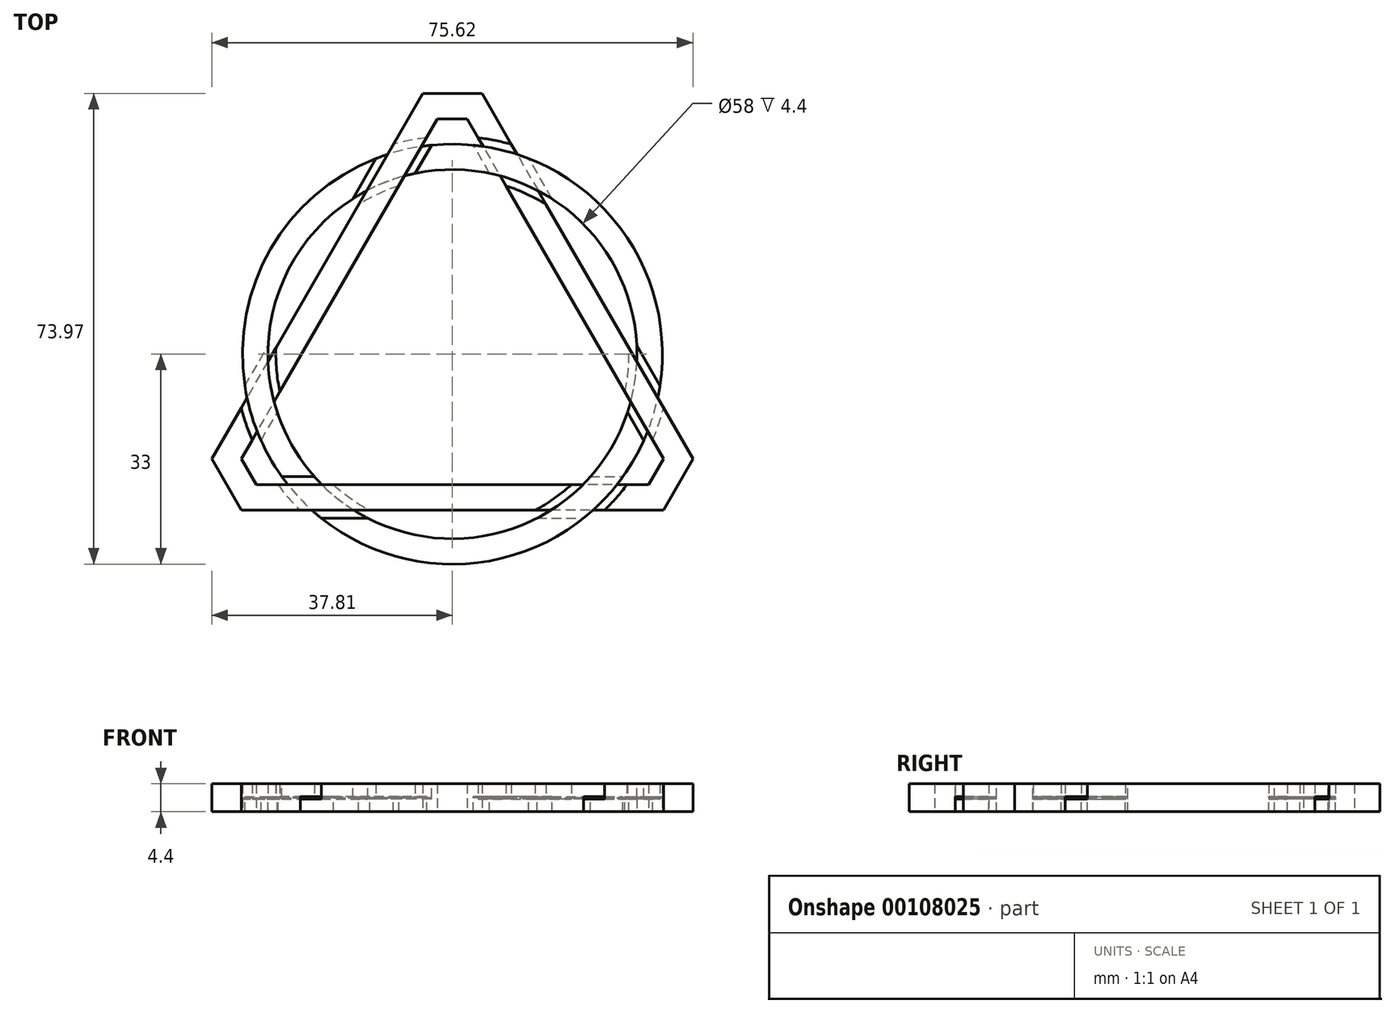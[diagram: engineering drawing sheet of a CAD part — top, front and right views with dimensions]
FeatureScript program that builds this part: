
annotation { "Feature Type Name" : "Feature", "Feature Type Description" : "" }
export const myFeature = defineFeature(function(context is Context, id is Id, definition is map)
    precondition{}
    {
        {
            var Q0;
            Q0=qCreatedBy(makeId("Top.planeOp"),FACE);
            var sketch = newSketch(context, id + "F0", { "sketchPlane" : qUnion([Q0])});
            skCircle(sketch, "E0", {"center": v(0, 0) * mm, "radius": 29 * mm});
            skCircle(sketch, "E1", {"center": v(0, 0) * mm, "radius": 33 * mm});
            skCircle(sketch, "E2", {"center": v(0, 0) * mm, "radius": 27.75 * mm, "construction": true});
            skCircle(sketch, "E3", {"center": v(0, 0) * mm, "radius": 34.25 * mm, "construction": true});
            skLineSegment(sketch, "E4", {"start": v(0, 45.03) * mm, "end": v(39, -22.52) * mm, "construction": true});
            skLineSegment(sketch, "E5", {"start": v(39, -22.52) * mm, "end": v(-39, -22.52) * mm, "construction": true});
            skLineSegment(sketch, "E6", {"start": v(-39, -22.52) * mm, "end": v(0, 45.03) * mm, "construction": true});
            skLineSegment(sketch, "E7", {"start": v(-3.5, 38.97) * mm, "end": v(3.5, 38.97) * mm, "construction": true});
            skLineSegment(sketch, "E8", {"start": v(35.5, -16.45) * mm, "end": v(32, -22.52) * mm, "construction": true});
            skLineSegment(sketch, "E9", {"start": v(-35.5, -16.45) * mm, "end": v(-32, -22.52) * mm, "construction": true});
            skLineSegment(sketch, "E10", {"start": v(39, -22.52) * mm, "end": v(-19.5, 11.26) * mm, "construction": true});
            skLineSegment(sketch, "E11", {"start": v(3.5, 38.97) * mm, "end": v(35.5, -16.45) * mm, "construction": true});
            skLineSegment(sketch, "E12", {"start": v(32, -22.52) * mm, "end": v(-32, -22.52) * mm, "construction": true});
            skLineSegment(sketch, "E13", {"start": v(-35.5, -16.45) * mm, "end": v(-3.5, 38.97) * mm, "construction": true});
            skLineSegment(sketch, "E14.0", {"start": v(-33.2, -16.45) * mm, "end": v(-2.35, 36.97) * mm});
            skLineSegment(sketch, "E14.1", {"start": v(2.35, 36.97) * mm, "end": v(33.2, -16.45) * mm});
            skLineSegment(sketch, "E14.2", {"start": v(33.2, -16.45) * mm, "end": v(30.85, -20.52) * mm});
            skLineSegment(sketch, "E14.3", {"start": v(-2.35, 36.97) * mm, "end": v(2.35, 36.97) * mm});
            skLineSegment(sketch, "E14.4", {"start": v(30.85, -20.52) * mm, "end": v(-30.85, -20.52) * mm});
            skLineSegment(sketch, "E14.5", {"start": v(-33.2, -16.45) * mm, "end": v(-30.85, -20.52) * mm});
            skLineSegment(sketch, "E15.0", {"start": v(-31.75, -16.45) * mm, "end": v(-1.62, 35.72) * mm, "construction": true});
            skLineSegment(sketch, "E15.1", {"start": v(1.62, 35.72) * mm, "end": v(31.75, -16.45) * mm, "construction": true});
            skLineSegment(sketch, "E15.2", {"start": v(31.75, -16.45) * mm, "end": v(30.12, -19.27) * mm, "construction": true});
            skLineSegment(sketch, "E15.3", {"start": v(-1.62, 35.72) * mm, "end": v(1.62, 35.72) * mm, "construction": true});
            skLineSegment(sketch, "E15.4", {"start": v(30.12, -19.27) * mm, "end": v(-30.12, -19.27) * mm, "construction": true});
            skLineSegment(sketch, "E15.5", {"start": v(-31.75, -16.45) * mm, "end": v(-30.12, -19.27) * mm, "construction": true});
            skLineSegment(sketch, "E16.0", {"start": v(-37.8, -16.45) * mm, "end": v(-33.15, -24.52) * mm});
            skLineSegment(sketch, "E16.1", {"start": v(-4.65, 40.97) * mm, "end": v(4.65, 40.97) * mm});
            skLineSegment(sketch, "E16.2", {"start": v(4.65, 40.97) * mm, "end": v(37.8, -16.45) * mm});
            skLineSegment(sketch, "E16.3", {"start": v(-37.8, -16.45) * mm, "end": v(-4.65, 40.97) * mm});
            skLineSegment(sketch, "E16.4", {"start": v(37.8, -16.45) * mm, "end": v(33.15, -24.52) * mm});
            skLineSegment(sketch, "E16.5", {"start": v(33.15, -24.52) * mm, "end": v(-33.15, -24.52) * mm});
            skLineSegment(sketch, "E17.0", {"start": v(-39.25, -16.45) * mm, "end": v(-33.88, -25.77) * mm, "construction": true});
            skLineSegment(sketch, "E17.1", {"start": v(-5.38, 42.22) * mm, "end": v(5.38, 42.22) * mm, "construction": true});
            skLineSegment(sketch, "E17.2", {"start": v(5.38, 42.22) * mm, "end": v(39.25, -16.45) * mm, "construction": true});
            skLineSegment(sketch, "E17.3", {"start": v(-39.25, -16.45) * mm, "end": v(-5.38, 42.22) * mm, "construction": true});
            skLineSegment(sketch, "E17.4", {"start": v(39.25, -16.45) * mm, "end": v(33.88, -25.77) * mm, "construction": true});
            skLineSegment(sketch, "E17.5", {"start": v(33.88, -25.77) * mm, "end": v(-33.88, -25.77) * mm, "construction": true});
            skArc(sketch, "E18", {"start": v(9.27, 32.97) * mm, "mid": v(6.68, 33.6) * mm, "end": v(4.06, 34) * mm});
            skArc(sketch, "E19", {"start": v(-27.73, 1) * mm, "mid": v(-27.64, -2.48) * mm, "end": v(-27.11, -5.92) * mm});
            skArc(sketch, "E20", {"start": v(-33.2, -8.45) * mm, "mid": v(-32.43, -11) * mm, "end": v(-31.48, -13.5) * mm});
            skArc(sketch, "E21", {"start": v(13, -24.52) * mm, "mid": v(15.97, -22.7) * mm, "end": v(18.68, -20.52) * mm});
            skArc(sketch, "E22", {"start": v(23.92, -24.52) * mm, "mid": v(25.75, -22.58) * mm, "end": v(27.42, -20.52) * mm});
            skArc(sketch, "E23", {"start": v(14.73, 23.52) * mm, "mid": v(11.67, 25.18) * mm, "end": v(8.43, 26.44) * mm});
            skLineSegment(sketch, "E24", {"start": v(-3.29, 32.84) * mm, "end": v(-5.85, 28.4) * mm});
            skLineSegment(sketch, "E25", {"start": v(-12, 30.74) * mm, "end": v(-15.66, 24.4) * mm});
            skLineSegment(sketch, "E26", {"start": v(-26.8, -19.27) * mm, "end": v(-21.67, -19.27) * mm});
            skLineSegment(sketch, "E27", {"start": v(-20.62, -25.77) * mm, "end": v(-13.3, -25.77) * mm});
            skLineSegment(sketch, "E28", {"start": v(30.08, -13.57) * mm, "end": v(27.52, -9.14) * mm});
            skLineSegment(sketch, "E29", {"start": v(32.62, -4.97) * mm, "end": v(28.97, 1.36) * mm});
            skArc(sketch, "E30", {"start": v(-4.06, 34) * mm, "mid": v(-6.68, 33.6) * mm, "end": v(-9.27, 32.97) * mm});
            skArc(sketch, "E31", {"start": v(-8.43, 26.44) * mm, "mid": v(-11.67, 25.18) * mm, "end": v(-14.73, 23.52) * mm});
            skArc(sketch, "E32", {"start": v(-27.42, -20.52) * mm, "mid": v(-25.75, -22.58) * mm, "end": v(-23.92, -24.52) * mm});
            skArc(sketch, "E33", {"start": v(-18.68, -20.52) * mm, "mid": v(-15.97, -22.7) * mm, "end": v(-13, -24.52) * mm});
            skArc(sketch, "E34", {"start": v(27.11, -5.92) * mm, "mid": v(27.64, -2.48) * mm, "end": v(27.73, 1) * mm});
            skArc(sketch, "E35", {"start": v(31.48, -13.5) * mm, "mid": v(32.43, -11) * mm, "end": v(33.2, -8.45) * mm});
            skLineSegment(sketch, "E36", {"start": v(-32.62, -4.97) * mm, "end": v(-28.97, 1.36) * mm});
            skLineSegment(sketch, "E37", {"start": v(-30.08, -13.57) * mm, "end": v(-27.52, -9.14) * mm});
            skLineSegment(sketch, "E38", {"start": v(13.3, -25.77) * mm, "end": v(20.62, -25.77) * mm});
            skLineSegment(sketch, "E39", {"start": v(21.67, -19.27) * mm, "end": v(26.8, -19.27) * mm});
            skLineSegment(sketch, "E40", {"start": v(5.85, 28.4) * mm, "end": v(3.29, 32.84) * mm});
            skLineSegment(sketch, "E41", {"start": v(15.66, 24.4) * mm, "end": v(12, 30.74) * mm});
            skSolve(sketch);
        }
        {
            var Q0;
            {var subQ5=sQuery(id+"F0.wireOp",EDGE,"E19");Q0=makeQuery(id+"F0.imprint","IMPRINT",FACE,{"disambiguationData":[TD([[makeQuery(id+"F0.imprint","IMPRINT",EDGE,{"derivedFrom":subQ5}),1.0]])]});}
            var Q1;
            {var subQ0=sQuery(id+"F0.wireOp",EDGE,"E14.0");var subQ1=sQuery(id+"F0.wireOp",EDGE,"E0");var subQ2=makeQuery(id+"F0.imprint","INTERSECT",VERTEX,{"disambiguationData":[OD(0.0)],"derivedFrom":[subQ1,subQ0]});Q1=makeQuery(id+"F0.imprint","IMPRINT",FACE,{"disambiguationData":[TD([[makeQuery(id+"F0.imprint","IMPRINT",EDGE,{"disambiguationData":[TD([[subQ2,-1.0]])],"derivedFrom":subQ1}),-1.0]])]});}
            var Q2;
            {var subQ0=sQuery(id+"F0.wireOp",EDGE,"E14.3");Q2=makeQuery(id+"F0.imprint","IMPRINT",FACE,{"disambiguationData":[TD([[makeQuery(id+"F0.imprint","IMPRINT",EDGE,{"derivedFrom":subQ0}),1.0]])]});}
            var Q3;
            {var subQ0=sQuery(id+"F0.wireOp",EDGE,"E24");Q3=makeQuery(id+"F0.imprint","IMPRINT",FACE,{"disambiguationData":[TD([[makeQuery(id+"F0.imprint","IMPRINT",EDGE,{"derivedFrom":subQ0}),1.0]])]});}
            var Q4;
            {var subQ0=sQuery(id+"F0.wireOp",EDGE,"E16.2");var subQ1=sQuery(id+"F0.wireOp",EDGE,"E0");var subQ2=makeQuery(id+"F0.imprint","INTERSECT",VERTEX,{"disambiguationData":[OD(0.0)],"derivedFrom":[subQ1,subQ0]});Q4=makeQuery(id+"F0.imprint","IMPRINT",FACE,{"disambiguationData":[TD([[makeQuery(id+"F0.imprint","IMPRINT",EDGE,{"disambiguationData":[TD([[subQ2,-1.0]])],"derivedFrom":subQ1}),-1.0]])]});}
            var Q5;
            {var subQ0=sQuery(id+"F0.wireOp",EDGE,"E29");Q5=makeQuery(id+"F0.imprint","IMPRINT",FACE,{"disambiguationData":[TD([[makeQuery(id+"F0.imprint","IMPRINT",EDGE,{"derivedFrom":subQ0}),-1.0]])]});}
            var Q6;
            {var subQ5=sQuery(id+"F0.wireOp",EDGE,"E23");Q6=makeQuery(id+"F0.imprint","IMPRINT",FACE,{"disambiguationData":[TD([[makeQuery(id+"F0.imprint","IMPRINT",EDGE,{"derivedFrom":subQ5}),1.0]])]});}
            var Q7;
            {var subQ0=sQuery(id+"F0.wireOp",EDGE,"E14.1");var subQ1=sQuery(id+"F0.wireOp",EDGE,"E0");var subQ2=makeQuery(id+"F0.imprint","INTERSECT",VERTEX,{"disambiguationData":[OD(1.0)],"derivedFrom":[subQ1,subQ0]});Q7=makeQuery(id+"F0.imprint","IMPRINT",FACE,{"disambiguationData":[TD([[makeQuery(id+"F0.imprint","IMPRINT",EDGE,{"disambiguationData":[TD([[subQ2,-1.0]])],"derivedFrom":subQ1}),-1.0]])]});}
            var Q8;
            {var subQ1=sQuery(id+"F0.wireOp",EDGE,"E14.2");Q8=makeQuery(id+"F0.imprint","IMPRINT",FACE,{"disambiguationData":[TD([[makeQuery(id+"F0.imprint","IMPRINT",EDGE,{"derivedFrom":subQ1}),1.0]])]});}
            var Q9;
            {var subQ0=sQuery(id+"F0.wireOp",EDGE,"E28");Q9=makeQuery(id+"F0.imprint","IMPRINT",FACE,{"disambiguationData":[TD([[makeQuery(id+"F0.imprint","IMPRINT",EDGE,{"derivedFrom":subQ0}),1.0]])]});}
            var Q10;
            {var subQ0=sQuery(id+"F0.wireOp",EDGE,"E16.5");var subQ1=sQuery(id+"F0.wireOp",EDGE,"E0");var subQ2=makeQuery(id+"F0.imprint","INTERSECT",VERTEX,{"disambiguationData":[OD(1.0)],"derivedFrom":[subQ1,subQ0]});Q10=makeQuery(id+"F0.imprint","IMPRINT",FACE,{"disambiguationData":[TD([[makeQuery(id+"F0.imprint","IMPRINT",EDGE,{"disambiguationData":[TD([[subQ2,-1.0]])],"derivedFrom":subQ1}),-1.0]])]});}
            var Q11;
            {var subQ0=sQuery(id+"F0.wireOp",EDGE,"E27");Q11=makeQuery(id+"F0.imprint","IMPRINT",FACE,{"disambiguationData":[TD([[makeQuery(id+"F0.imprint","IMPRINT",EDGE,{"derivedFrom":subQ0}),-1.0]])]});}
            var Q12;
            {var subQ5=sQuery(id+"F0.wireOp",EDGE,"E21");Q12=makeQuery(id+"F0.imprint","IMPRINT",FACE,{"disambiguationData":[TD([[makeQuery(id+"F0.imprint","IMPRINT",EDGE,{"derivedFrom":subQ5}),1.0]])]});}
            var Q13;
            {var subQ0=sQuery(id+"F0.wireOp",EDGE,"E14.4");var subQ1=sQuery(id+"F0.wireOp",EDGE,"E0");var subQ2=makeQuery(id+"F0.imprint","INTERSECT",VERTEX,{"disambiguationData":[OD(0.0)],"derivedFrom":[subQ1,subQ0]});Q13=makeQuery(id+"F0.imprint","IMPRINT",FACE,{"disambiguationData":[TD([[makeQuery(id+"F0.imprint","IMPRINT",EDGE,{"disambiguationData":[TD([[subQ2,-1.0]])],"derivedFrom":subQ1}),-1.0]])]});}
            var Q14;
            {var subQ0=sQuery(id+"F0.wireOp",EDGE,"E14.5");Q14=makeQuery(id+"F0.imprint","IMPRINT",FACE,{"disambiguationData":[TD([[makeQuery(id+"F0.imprint","IMPRINT",EDGE,{"derivedFrom":subQ0}),-1.0]])]});}
            var Q15;
            {var subQ0=sQuery(id+"F0.wireOp",EDGE,"E26");Q15=makeQuery(id+"F0.imprint","IMPRINT",FACE,{"disambiguationData":[TD([[makeQuery(id+"F0.imprint","IMPRINT",EDGE,{"derivedFrom":subQ0}),1.0]])]});}
            var Q16;
            {var subQ0=sQuery(id+"F0.wireOp",EDGE,"E16.3");var subQ1=sQuery(id+"F0.wireOp",EDGE,"E0");var subQ2=makeQuery(id+"F0.imprint","INTERSECT",VERTEX,{"disambiguationData":[OD(1.0)],"derivedFrom":[subQ1,subQ0]});Q16=makeQuery(id+"F0.imprint","IMPRINT",FACE,{"disambiguationData":[TD([[makeQuery(id+"F0.imprint","IMPRINT",EDGE,{"disambiguationData":[TD([[subQ2,-1.0]])],"derivedFrom":subQ1}),-1.0]])]});}
            var Q17;
            {var subQ0=sQuery(id+"F0.wireOp",EDGE,"E25");Q17=makeQuery(id+"F0.imprint","IMPRINT",FACE,{"disambiguationData":[TD([[makeQuery(id+"F0.imprint","IMPRINT",EDGE,{"derivedFrom":subQ0}),-1.0]])]});}
            var Q18;
            {var subQ0=sQuery(id+"F0.wireOp",EDGE,"E36");Q18=makeQuery(id+"F0.imprint","IMPRINT",FACE,{"disambiguationData":[TD([[makeQuery(id+"F0.imprint","IMPRINT",EDGE,{"derivedFrom":subQ0}),-1.0]])]});}
            var Q19;
            {var subQ0=sQuery(id+"F0.wireOp",EDGE,"E37");Q19=makeQuery(id+"F0.imprint","IMPRINT",FACE,{"disambiguationData":[TD([[makeQuery(id+"F0.imprint","IMPRINT",EDGE,{"derivedFrom":subQ0}),1.0]])]});}
            var Q20;
            {var subQ5=sQuery(id+"F0.wireOp",EDGE,"E32");Q20=makeQuery(id+"F0.imprint","IMPRINT",FACE,{"disambiguationData":[TD([[makeQuery(id+"F0.imprint","IMPRINT",EDGE,{"derivedFrom":subQ5}),1.0]])]});}
            var Q21;
            {var subQ5=sQuery(id+"F0.wireOp",EDGE,"E33");Q21=makeQuery(id+"F0.imprint","IMPRINT",FACE,{"disambiguationData":[TD([[makeQuery(id+"F0.imprint","IMPRINT",EDGE,{"derivedFrom":subQ5}),-1.0]])]});}
            var Q22;
            {var subQ0=sQuery(id+"F0.wireOp",EDGE,"E38");Q22=makeQuery(id+"F0.imprint","IMPRINT",FACE,{"disambiguationData":[TD([[makeQuery(id+"F0.imprint","IMPRINT",EDGE,{"derivedFrom":subQ0}),1.0]])]});}
            var Q23;
            {var subQ0=sQuery(id+"F0.wireOp",EDGE,"E39");Q23=makeQuery(id+"F0.imprint","IMPRINT",FACE,{"disambiguationData":[TD([[makeQuery(id+"F0.imprint","IMPRINT",EDGE,{"derivedFrom":subQ0}),-1.0]])]});}
            var Q24;
            {var subQ5=sQuery(id+"F0.wireOp",EDGE,"E34");Q24=makeQuery(id+"F0.imprint","IMPRINT",FACE,{"disambiguationData":[TD([[makeQuery(id+"F0.imprint","IMPRINT",EDGE,{"derivedFrom":subQ5}),-1.0]])]});}
            var Q25;
            {var subQ5=sQuery(id+"F0.wireOp",EDGE,"E35");Q25=makeQuery(id+"F0.imprint","IMPRINT",FACE,{"disambiguationData":[TD([[makeQuery(id+"F0.imprint","IMPRINT",EDGE,{"derivedFrom":subQ5}),1.0]])]});}
            var Q26;
            {var subQ0=sQuery(id+"F0.wireOp",EDGE,"E41");Q26=makeQuery(id+"F0.imprint","IMPRINT",FACE,{"disambiguationData":[TD([[makeQuery(id+"F0.imprint","IMPRINT",EDGE,{"derivedFrom":subQ0}),1.0]])]});}
            var Q27;
            {var subQ0=sQuery(id+"F0.wireOp",EDGE,"E40");Q27=makeQuery(id+"F0.imprint","IMPRINT",FACE,{"disambiguationData":[TD([[makeQuery(id+"F0.imprint","IMPRINT",EDGE,{"derivedFrom":subQ0}),-1.0]])]});}
            var Q28;
            {var subQ5=sQuery(id+"F0.wireOp",EDGE,"E30");Q28=makeQuery(id+"F0.imprint","IMPRINT",FACE,{"disambiguationData":[TD([[makeQuery(id+"F0.imprint","IMPRINT",EDGE,{"derivedFrom":subQ5}),1.0]])]});}
            var Q29;
            {var subQ5=sQuery(id+"F0.wireOp",EDGE,"E31");Q29=makeQuery(id+"F0.imprint","IMPRINT",FACE,{"disambiguationData":[TD([[makeQuery(id+"F0.imprint","IMPRINT",EDGE,{"derivedFrom":subQ5}),-1.0]])]});}
            extrude(context, id + "F1", {"entities" : qUnion([Q0, Q1, Q2, Q3, Q4, Q5, Q6, Q7, Q8, Q9, Q10, Q11, Q12, Q13, Q14, Q15, Q16, Q17, Q18, Q19, Q20, Q21, Q22, Q23, Q24, Q25, Q26, Q27, Q28, Q29]), "depth" : 2.2 * mm});
        }
        {
            var Q0;
            {var subQ0=sQuery(id+"F0.wireOp",EDGE,"E25");Q0=makeQuery(id+"F0.imprint","IMPRINT",FACE,{"disambiguationData":[TD([[makeQuery(id+"F0.imprint","IMPRINT",EDGE,{"derivedFrom":subQ0}),-1.0]])]});}
            var Q1;
            {var subQ1=sQuery(id+"F0.wireOp",EDGE,"E14.3");Q1=makeQuery(id+"F0.imprint","IMPRINT",FACE,{"disambiguationData":[TD([[makeQuery(id+"F0.imprint","IMPRINT",EDGE,{"derivedFrom":subQ1}),1.0]])]});}
            var Q2;
            {var subQ0=sQuery(id+"F0.wireOp",EDGE,"E29");Q2=makeQuery(id+"F0.imprint","IMPRINT",FACE,{"disambiguationData":[TD([[makeQuery(id+"F0.imprint","IMPRINT",EDGE,{"derivedFrom":subQ0}),-1.0]])]});}
            var Q3;
            {var subQ5=sQuery(id+"F0.wireOp",EDGE,"E14.2");Q3=makeQuery(id+"F0.imprint","IMPRINT",FACE,{"disambiguationData":[TD([[makeQuery(id+"F0.imprint","IMPRINT",EDGE,{"derivedFrom":subQ5}),1.0]])]});}
            var Q4;
            {var subQ0=sQuery(id+"F0.wireOp",EDGE,"E27");Q4=makeQuery(id+"F0.imprint","IMPRINT",FACE,{"disambiguationData":[TD([[makeQuery(id+"F0.imprint","IMPRINT",EDGE,{"derivedFrom":subQ0}),-1.0]])]});}
            var Q5;
            {var subQ1=sQuery(id+"F0.wireOp",EDGE,"E14.5");Q5=makeQuery(id+"F0.imprint","IMPRINT",FACE,{"disambiguationData":[TD([[makeQuery(id+"F0.imprint","IMPRINT",EDGE,{"derivedFrom":subQ1}),-1.0]])]});}
            var Q6;
            {var subQ0=sQuery(id+"F0.wireOp",EDGE,"E19");Q6=makeQuery(id+"F0.imprint","IMPRINT",FACE,{"disambiguationData":[TD([[makeQuery(id+"F0.imprint","IMPRINT",EDGE,{"derivedFrom":subQ0}),1.0]])]});}
            var Q7;
            {var subQ0=sQuery(id+"F0.wireOp",EDGE,"E23");Q7=makeQuery(id+"F0.imprint","IMPRINT",FACE,{"disambiguationData":[TD([[makeQuery(id+"F0.imprint","IMPRINT",EDGE,{"derivedFrom":subQ0}),1.0]])]});}
            var Q8;
            {var subQ0=sQuery(id+"F0.wireOp",EDGE,"E24");Q8=makeQuery(id+"F0.imprint","IMPRINT",FACE,{"disambiguationData":[TD([[makeQuery(id+"F0.imprint","IMPRINT",EDGE,{"derivedFrom":subQ0}),1.0]])]});}
            var Q9;
            {var subQ0=sQuery(id+"F0.wireOp",EDGE,"E26");Q9=makeQuery(id+"F0.imprint","IMPRINT",FACE,{"disambiguationData":[TD([[makeQuery(id+"F0.imprint","IMPRINT",EDGE,{"derivedFrom":subQ0}),1.0]])]});}
            var Q10;
            {var subQ0=sQuery(id+"F0.wireOp",EDGE,"E28");Q10=makeQuery(id+"F0.imprint","IMPRINT",FACE,{"disambiguationData":[TD([[makeQuery(id+"F0.imprint","IMPRINT",EDGE,{"derivedFrom":subQ0}),1.0]])]});}
            var Q11;
            {var subQ0=sQuery(id+"F0.wireOp",EDGE,"E21");Q11=makeQuery(id+"F0.imprint","IMPRINT",FACE,{"disambiguationData":[TD([[makeQuery(id+"F0.imprint","IMPRINT",EDGE,{"derivedFrom":subQ0}),1.0]])]});}
            var Q12;
            {var subQ0=sQuery(id+"F0.wireOp",EDGE,"E24");Q12=makeQuery(id+"F0.imprint","IMPRINT",FACE,{"disambiguationData":[TD([[makeQuery(id+"F0.imprint","IMPRINT",EDGE,{"derivedFrom":subQ0}),-1.0]])]});}
            var Q13;
            {var subQ0=sQuery(id+"F0.wireOp",EDGE,"E14.0");var subQ1=sQuery(id+"F0.wireOp",EDGE,"E0");var subQ2=makeQuery(id+"F0.imprint","INTERSECT",VERTEX,{"disambiguationData":[OD(0.0)],"derivedFrom":[subQ1,subQ0]});Q13=makeQuery(id+"F0.imprint","IMPRINT",FACE,{"disambiguationData":[TD([[makeQuery(id+"F0.imprint","IMPRINT",EDGE,{"disambiguationData":[TD([[subQ2,-1.0]])],"derivedFrom":subQ1}),-1.0]])]});}
            var Q14;
            {var subQ0=sQuery(id+"F0.wireOp",EDGE,"E25");Q14=makeQuery(id+"F0.imprint","IMPRINT",FACE,{"disambiguationData":[TD([[makeQuery(id+"F0.imprint","IMPRINT",EDGE,{"derivedFrom":subQ0}),1.0]])]});}
            var Q15;
            {var subQ5=sQuery(id+"F0.wireOp",EDGE,"E18");Q15=makeQuery(id+"F0.imprint","IMPRINT",FACE,{"disambiguationData":[TD([[makeQuery(id+"F0.imprint","IMPRINT",EDGE,{"derivedFrom":subQ5}),1.0]])]});}
            var Q16;
            {var subQ0=sQuery(id+"F0.wireOp",EDGE,"E16.2");var subQ1=sQuery(id+"F0.wireOp",EDGE,"E0");var subQ2=makeQuery(id+"F0.imprint","INTERSECT",VERTEX,{"disambiguationData":[OD(0.0)],"derivedFrom":[subQ1,subQ0]});Q16=makeQuery(id+"F0.imprint","IMPRINT",FACE,{"disambiguationData":[TD([[makeQuery(id+"F0.imprint","IMPRINT",EDGE,{"disambiguationData":[TD([[subQ2,-1.0]])],"derivedFrom":subQ1}),-1.0]])]});}
            var Q17;
            {var subQ5=sQuery(id+"F0.wireOp",EDGE,"E23");Q17=makeQuery(id+"F0.imprint","IMPRINT",FACE,{"disambiguationData":[TD([[makeQuery(id+"F0.imprint","IMPRINT",EDGE,{"derivedFrom":subQ5}),-1.0]])]});}
            var Q18;
            {var subQ0=sQuery(id+"F0.wireOp",EDGE,"E14.1");var subQ1=sQuery(id+"F0.wireOp",EDGE,"E0");var subQ2=makeQuery(id+"F0.imprint","INTERSECT",VERTEX,{"disambiguationData":[OD(1.0)],"derivedFrom":[subQ1,subQ0]});Q18=makeQuery(id+"F0.imprint","IMPRINT",FACE,{"disambiguationData":[TD([[makeQuery(id+"F0.imprint","IMPRINT",EDGE,{"disambiguationData":[TD([[subQ2,-1.0]])],"derivedFrom":subQ1}),-1.0]])]});}
            var Q19;
            {var subQ0=sQuery(id+"F0.wireOp",EDGE,"E28");Q19=makeQuery(id+"F0.imprint","IMPRINT",FACE,{"disambiguationData":[TD([[makeQuery(id+"F0.imprint","IMPRINT",EDGE,{"derivedFrom":subQ0}),-1.0]])]});}
            var Q20;
            {var subQ0=sQuery(id+"F0.wireOp",EDGE,"E29");Q20=makeQuery(id+"F0.imprint","IMPRINT",FACE,{"disambiguationData":[TD([[makeQuery(id+"F0.imprint","IMPRINT",EDGE,{"derivedFrom":subQ0}),1.0]])]});}
            var Q21;
            {var subQ5=sQuery(id+"F0.wireOp",EDGE,"E22");Q21=makeQuery(id+"F0.imprint","IMPRINT",FACE,{"disambiguationData":[TD([[makeQuery(id+"F0.imprint","IMPRINT",EDGE,{"derivedFrom":subQ5}),1.0]])]});}
            var Q22;
            {var subQ0=sQuery(id+"F0.wireOp",EDGE,"E16.5");var subQ1=sQuery(id+"F0.wireOp",EDGE,"E0");var subQ2=makeQuery(id+"F0.imprint","INTERSECT",VERTEX,{"disambiguationData":[OD(1.0)],"derivedFrom":[subQ1,subQ0]});Q22=makeQuery(id+"F0.imprint","IMPRINT",FACE,{"disambiguationData":[TD([[makeQuery(id+"F0.imprint","IMPRINT",EDGE,{"disambiguationData":[TD([[subQ2,-1.0]])],"derivedFrom":subQ1}),-1.0]])]});}
            var Q23;
            {var subQ5=sQuery(id+"F0.wireOp",EDGE,"E21");Q23=makeQuery(id+"F0.imprint","IMPRINT",FACE,{"disambiguationData":[TD([[makeQuery(id+"F0.imprint","IMPRINT",EDGE,{"derivedFrom":subQ5}),-1.0]])]});}
            var Q24;
            {var subQ0=sQuery(id+"F0.wireOp",EDGE,"E27");Q24=makeQuery(id+"F0.imprint","IMPRINT",FACE,{"disambiguationData":[TD([[makeQuery(id+"F0.imprint","IMPRINT",EDGE,{"derivedFrom":subQ0}),1.0]])]});}
            var Q25;
            {var subQ0=sQuery(id+"F0.wireOp",EDGE,"E14.4");var subQ1=sQuery(id+"F0.wireOp",EDGE,"E0");var subQ2=makeQuery(id+"F0.imprint","INTERSECT",VERTEX,{"disambiguationData":[OD(0.0)],"derivedFrom":[subQ1,subQ0]});Q25=makeQuery(id+"F0.imprint","IMPRINT",FACE,{"disambiguationData":[TD([[makeQuery(id+"F0.imprint","IMPRINT",EDGE,{"disambiguationData":[TD([[subQ2,-1.0]])],"derivedFrom":subQ1}),-1.0]])]});}
            var Q26;
            {var subQ0=sQuery(id+"F0.wireOp",EDGE,"E26");Q26=makeQuery(id+"F0.imprint","IMPRINT",FACE,{"disambiguationData":[TD([[makeQuery(id+"F0.imprint","IMPRINT",EDGE,{"derivedFrom":subQ0}),-1.0]])]});}
            var Q27;
            {var subQ5=sQuery(id+"F0.wireOp",EDGE,"E20");Q27=makeQuery(id+"F0.imprint","IMPRINT",FACE,{"disambiguationData":[TD([[makeQuery(id+"F0.imprint","IMPRINT",EDGE,{"derivedFrom":subQ5}),1.0]])]});}
            var Q28;
            {var subQ0=sQuery(id+"F0.wireOp",EDGE,"E16.3");var subQ1=sQuery(id+"F0.wireOp",EDGE,"E0");var subQ2=makeQuery(id+"F0.imprint","INTERSECT",VERTEX,{"disambiguationData":[OD(1.0)],"derivedFrom":[subQ1,subQ0]});Q28=makeQuery(id+"F0.imprint","IMPRINT",FACE,{"disambiguationData":[TD([[makeQuery(id+"F0.imprint","IMPRINT",EDGE,{"disambiguationData":[TD([[subQ2,-1.0]])],"derivedFrom":subQ1}),-1.0]])]});}
            var Q29;
            {var subQ5=sQuery(id+"F0.wireOp",EDGE,"E19");Q29=makeQuery(id+"F0.imprint","IMPRINT",FACE,{"disambiguationData":[TD([[makeQuery(id+"F0.imprint","IMPRINT",EDGE,{"derivedFrom":subQ5}),-1.0]])]});}
            extrude(context, id + "F2", {"entities" : qUnion([Q0, Q1, Q2, Q3, Q4, Q5, Q6, Q7, Q8, Q9, Q10, Q11, Q12, Q13, Q14, Q15, Q16, Q17, Q18, Q19, Q20, Q21, Q22, Q23, Q24, Q25, Q26, Q27, Q28, Q29]), "operationType" : NewBodyOperationType.ADD, "oppositeDirection" : true, "depth" : 2.2 * mm});
        }
        {
            var Q0;
            {var subQ0=sQuery(id+"F0.wireOp",EDGE,"E14.0");var subQ1=sQuery(id+"F0.wireOp",EDGE,"E0");var subQ2=makeQuery(id+"F0.imprint","INTERSECT",VERTEX,{"disambiguationData":[OD(0.0)],"derivedFrom":[subQ1,subQ0]});Q0=makeQuery(id+"F0.imprint","IMPRINT",FACE,{"disambiguationData":[TD([[makeQuery(id+"F0.imprint","IMPRINT",EDGE,{"disambiguationData":[TD([[subQ2,-1.0]])],"derivedFrom":subQ1}),-1.0]])]});}
            var Q1;
            {var subQ0=sQuery(id+"F0.wireOp",EDGE,"E16.2");var subQ1=sQuery(id+"F0.wireOp",EDGE,"E0");var subQ2=makeQuery(id+"F0.imprint","INTERSECT",VERTEX,{"disambiguationData":[OD(0.0)],"derivedFrom":[subQ1,subQ0]});Q1=makeQuery(id+"F0.imprint","IMPRINT",FACE,{"disambiguationData":[TD([[makeQuery(id+"F0.imprint","IMPRINT",EDGE,{"disambiguationData":[TD([[subQ2,-1.0]])],"derivedFrom":subQ1}),-1.0]])]});}
            var Q2;
            {var subQ0=sQuery(id+"F0.wireOp",EDGE,"E14.1");var subQ1=sQuery(id+"F0.wireOp",EDGE,"E0");var subQ2=makeQuery(id+"F0.imprint","INTERSECT",VERTEX,{"disambiguationData":[OD(1.0)],"derivedFrom":[subQ1,subQ0]});Q2=makeQuery(id+"F0.imprint","IMPRINT",FACE,{"disambiguationData":[TD([[makeQuery(id+"F0.imprint","IMPRINT",EDGE,{"disambiguationData":[TD([[subQ2,-1.0]])],"derivedFrom":subQ1}),-1.0]])]});}
            var Q3;
            {var subQ0=sQuery(id+"F0.wireOp",EDGE,"E16.5");var subQ1=sQuery(id+"F0.wireOp",EDGE,"E0");var subQ2=makeQuery(id+"F0.imprint","INTERSECT",VERTEX,{"disambiguationData":[OD(1.0)],"derivedFrom":[subQ1,subQ0]});Q3=makeQuery(id+"F0.imprint","IMPRINT",FACE,{"disambiguationData":[TD([[makeQuery(id+"F0.imprint","IMPRINT",EDGE,{"disambiguationData":[TD([[subQ2,-1.0]])],"derivedFrom":subQ1}),-1.0]])]});}
            var Q4;
            {var subQ0=sQuery(id+"F0.wireOp",EDGE,"E14.4");var subQ1=sQuery(id+"F0.wireOp",EDGE,"E0");var subQ2=makeQuery(id+"F0.imprint","INTERSECT",VERTEX,{"disambiguationData":[OD(0.0)],"derivedFrom":[subQ1,subQ0]});Q4=makeQuery(id+"F0.imprint","IMPRINT",FACE,{"disambiguationData":[TD([[makeQuery(id+"F0.imprint","IMPRINT",EDGE,{"disambiguationData":[TD([[subQ2,-1.0]])],"derivedFrom":subQ1}),-1.0]])]});}
            var Q5;
            {var subQ0=sQuery(id+"F0.wireOp",EDGE,"E16.3");var subQ1=sQuery(id+"F0.wireOp",EDGE,"E0");var subQ2=makeQuery(id+"F0.imprint","INTERSECT",VERTEX,{"disambiguationData":[OD(1.0)],"derivedFrom":[subQ1,subQ0]});Q5=makeQuery(id+"F0.imprint","IMPRINT",FACE,{"disambiguationData":[TD([[makeQuery(id+"F0.imprint","IMPRINT",EDGE,{"disambiguationData":[TD([[subQ2,-1.0]])],"derivedFrom":subQ1}),-1.0]])]});}
            var Q6;
            {var subQ0=sQuery(id+"F0.wireOp",EDGE,"E25");Q6=makeQuery(id+"F0.imprint","IMPRINT",FACE,{"disambiguationData":[TD([[makeQuery(id+"F0.imprint","IMPRINT",EDGE,{"derivedFrom":subQ0}),1.0]])]});}
            var Q7;
            {var subQ5=sQuery(id+"F0.wireOp",EDGE,"E30");Q7=makeQuery(id+"F0.imprint","IMPRINT",FACE,{"disambiguationData":[TD([[makeQuery(id+"F0.imprint","IMPRINT",EDGE,{"derivedFrom":subQ5}),1.0]])]});}
            var Q8;
            {var subQ0=sQuery(id+"F0.wireOp",EDGE,"E24");Q8=makeQuery(id+"F0.imprint","IMPRINT",FACE,{"disambiguationData":[TD([[makeQuery(id+"F0.imprint","IMPRINT",EDGE,{"derivedFrom":subQ0}),-1.0]])]});}
            var Q9;
            {var subQ5=sQuery(id+"F0.wireOp",EDGE,"E31");Q9=makeQuery(id+"F0.imprint","IMPRINT",FACE,{"disambiguationData":[TD([[makeQuery(id+"F0.imprint","IMPRINT",EDGE,{"derivedFrom":subQ5}),-1.0]])]});}
            var Q10;
            {var subQ5=sQuery(id+"F0.wireOp",EDGE,"E18");Q10=makeQuery(id+"F0.imprint","IMPRINT",FACE,{"disambiguationData":[TD([[makeQuery(id+"F0.imprint","IMPRINT",EDGE,{"derivedFrom":subQ5}),1.0]])]});}
            var Q11;
            {var subQ0=sQuery(id+"F0.wireOp",EDGE,"E41");Q11=makeQuery(id+"F0.imprint","IMPRINT",FACE,{"disambiguationData":[TD([[makeQuery(id+"F0.imprint","IMPRINT",EDGE,{"derivedFrom":subQ0}),1.0]])]});}
            var Q12;
            {var subQ5=sQuery(id+"F0.wireOp",EDGE,"E23");Q12=makeQuery(id+"F0.imprint","IMPRINT",FACE,{"disambiguationData":[TD([[makeQuery(id+"F0.imprint","IMPRINT",EDGE,{"derivedFrom":subQ5}),-1.0]])]});}
            var Q13;
            {var subQ0=sQuery(id+"F0.wireOp",EDGE,"E40");Q13=makeQuery(id+"F0.imprint","IMPRINT",FACE,{"disambiguationData":[TD([[makeQuery(id+"F0.imprint","IMPRINT",EDGE,{"derivedFrom":subQ0}),-1.0]])]});}
            var Q14;
            {var subQ0=sQuery(id+"F0.wireOp",EDGE,"E29");Q14=makeQuery(id+"F0.imprint","IMPRINT",FACE,{"disambiguationData":[TD([[makeQuery(id+"F0.imprint","IMPRINT",EDGE,{"derivedFrom":subQ0}),1.0]])]});}
            var Q15;
            {var subQ5=sQuery(id+"F0.wireOp",EDGE,"E34");Q15=makeQuery(id+"F0.imprint","IMPRINT",FACE,{"disambiguationData":[TD([[makeQuery(id+"F0.imprint","IMPRINT",EDGE,{"derivedFrom":subQ5}),-1.0]])]});}
            var Q16;
            {var subQ0=sQuery(id+"F0.wireOp",EDGE,"E28");Q16=makeQuery(id+"F0.imprint","IMPRINT",FACE,{"disambiguationData":[TD([[makeQuery(id+"F0.imprint","IMPRINT",EDGE,{"derivedFrom":subQ0}),-1.0]])]});}
            var Q17;
            {var subQ5=sQuery(id+"F0.wireOp",EDGE,"E35");Q17=makeQuery(id+"F0.imprint","IMPRINT",FACE,{"disambiguationData":[TD([[makeQuery(id+"F0.imprint","IMPRINT",EDGE,{"derivedFrom":subQ5}),1.0]])]});}
            var Q18;
            {var subQ5=sQuery(id+"F0.wireOp",EDGE,"E22");Q18=makeQuery(id+"F0.imprint","IMPRINT",FACE,{"disambiguationData":[TD([[makeQuery(id+"F0.imprint","IMPRINT",EDGE,{"derivedFrom":subQ5}),1.0]])]});}
            var Q19;
            {var subQ0=sQuery(id+"F0.wireOp",EDGE,"E39");Q19=makeQuery(id+"F0.imprint","IMPRINT",FACE,{"disambiguationData":[TD([[makeQuery(id+"F0.imprint","IMPRINT",EDGE,{"derivedFrom":subQ0}),-1.0]])]});}
            var Q20;
            {var subQ5=sQuery(id+"F0.wireOp",EDGE,"E21");Q20=makeQuery(id+"F0.imprint","IMPRINT",FACE,{"disambiguationData":[TD([[makeQuery(id+"F0.imprint","IMPRINT",EDGE,{"derivedFrom":subQ5}),-1.0]])]});}
            var Q21;
            {var subQ0=sQuery(id+"F0.wireOp",EDGE,"E38");Q21=makeQuery(id+"F0.imprint","IMPRINT",FACE,{"disambiguationData":[TD([[makeQuery(id+"F0.imprint","IMPRINT",EDGE,{"derivedFrom":subQ0}),1.0]])]});}
            var Q22;
            {var subQ0=sQuery(id+"F0.wireOp",EDGE,"E27");Q22=makeQuery(id+"F0.imprint","IMPRINT",FACE,{"disambiguationData":[TD([[makeQuery(id+"F0.imprint","IMPRINT",EDGE,{"derivedFrom":subQ0}),1.0]])]});}
            var Q23;
            {var subQ5=sQuery(id+"F0.wireOp",EDGE,"E33");Q23=makeQuery(id+"F0.imprint","IMPRINT",FACE,{"disambiguationData":[TD([[makeQuery(id+"F0.imprint","IMPRINT",EDGE,{"derivedFrom":subQ5}),-1.0]])]});}
            var Q24;
            {var subQ0=sQuery(id+"F0.wireOp",EDGE,"E26");Q24=makeQuery(id+"F0.imprint","IMPRINT",FACE,{"disambiguationData":[TD([[makeQuery(id+"F0.imprint","IMPRINT",EDGE,{"derivedFrom":subQ0}),-1.0]])]});}
            var Q25;
            {var subQ5=sQuery(id+"F0.wireOp",EDGE,"E32");Q25=makeQuery(id+"F0.imprint","IMPRINT",FACE,{"disambiguationData":[TD([[makeQuery(id+"F0.imprint","IMPRINT",EDGE,{"derivedFrom":subQ5}),1.0]])]});}
            var Q26;
            {var subQ5=sQuery(id+"F0.wireOp",EDGE,"E20");Q26=makeQuery(id+"F0.imprint","IMPRINT",FACE,{"disambiguationData":[TD([[makeQuery(id+"F0.imprint","IMPRINT",EDGE,{"derivedFrom":subQ5}),1.0]])]});}
            var Q27;
            {var subQ0=sQuery(id+"F0.wireOp",EDGE,"E37");Q27=makeQuery(id+"F0.imprint","IMPRINT",FACE,{"disambiguationData":[TD([[makeQuery(id+"F0.imprint","IMPRINT",EDGE,{"derivedFrom":subQ0}),1.0]])]});}
            var Q28;
            {var subQ5=sQuery(id+"F0.wireOp",EDGE,"E19");Q28=makeQuery(id+"F0.imprint","IMPRINT",FACE,{"disambiguationData":[TD([[makeQuery(id+"F0.imprint","IMPRINT",EDGE,{"derivedFrom":subQ5}),-1.0]])]});}
            var Q29;
            {var subQ0=sQuery(id+"F0.wireOp",EDGE,"E36");Q29=makeQuery(id+"F0.imprint","IMPRINT",FACE,{"disambiguationData":[TD([[makeQuery(id+"F0.imprint","IMPRINT",EDGE,{"derivedFrom":subQ0}),-1.0]])]});}
            extrude(context, id + "F3", {"entities" : qUnion([Q0, Q1, Q2, Q3, Q4, Q5, Q6, Q7, Q8, Q9, Q10, Q11, Q12, Q13, Q14, Q15, Q16, Q17, Q18, Q19, Q20, Q21, Q22, Q23, Q24, Q25, Q26, Q27, Q28, Q29]), "operationType" : NewBodyOperationType.REMOVE, "endBound" : BoundingType.SYMMETRIC, "oppositeDirection" : true, "depth" : 0.4 * mm});
        }
        {
            var Q0;
            {var subQ0=sQuery(id+"F0.wireOp",EDGE,"E24");Q0=makeQuery(id+"F0.imprint","IMPRINT",FACE,{"disambiguationData":[TD([[makeQuery(id+"F0.imprint","IMPRINT",EDGE,{"derivedFrom":subQ0}),-1.0]])]});}
            var Q1;
            {var subQ0=sQuery(id+"F0.wireOp",EDGE,"E37");Q1=makeQuery(id+"F0.imprint","IMPRINT",FACE,{"disambiguationData":[TD([[makeQuery(id+"F0.imprint","IMPRINT",EDGE,{"derivedFrom":subQ0}),1.0]])]});}
            var Q2;
            {var subQ0=sQuery(id+"F0.wireOp",EDGE,"E39");Q2=makeQuery(id+"F0.imprint","IMPRINT",FACE,{"disambiguationData":[TD([[makeQuery(id+"F0.imprint","IMPRINT",EDGE,{"derivedFrom":subQ0}),-1.0]])]});}
            var Q3;
            {var subQ0=sQuery(id+"F0.wireOp",EDGE,"E25");Q3=makeQuery(id+"F0.imprint","IMPRINT",FACE,{"disambiguationData":[TD([[makeQuery(id+"F0.imprint","IMPRINT",EDGE,{"derivedFrom":subQ0}),1.0]])]});}
            var Q4;
            {var subQ5=sQuery(id+"F0.wireOp",EDGE,"E30");Q4=makeQuery(id+"F0.imprint","IMPRINT",FACE,{"disambiguationData":[TD([[makeQuery(id+"F0.imprint","IMPRINT",EDGE,{"derivedFrom":subQ5}),1.0]])]});}
            var Q5;
            {var subQ5=sQuery(id+"F0.wireOp",EDGE,"E31");Q5=makeQuery(id+"F0.imprint","IMPRINT",FACE,{"disambiguationData":[TD([[makeQuery(id+"F0.imprint","IMPRINT",EDGE,{"derivedFrom":subQ5}),-1.0]])]});}
            var Q6;
            {var subQ5=sQuery(id+"F0.wireOp",EDGE,"E18");Q6=makeQuery(id+"F0.imprint","IMPRINT",FACE,{"disambiguationData":[TD([[makeQuery(id+"F0.imprint","IMPRINT",EDGE,{"derivedFrom":subQ5}),1.0]])]});}
            var Q7;
            {var subQ0=sQuery(id+"F0.wireOp",EDGE,"E40");Q7=makeQuery(id+"F0.imprint","IMPRINT",FACE,{"disambiguationData":[TD([[makeQuery(id+"F0.imprint","IMPRINT",EDGE,{"derivedFrom":subQ0}),-1.0]])]});}
            var Q8;
            {var subQ0=sQuery(id+"F0.wireOp",EDGE,"E41");Q8=makeQuery(id+"F0.imprint","IMPRINT",FACE,{"disambiguationData":[TD([[makeQuery(id+"F0.imprint","IMPRINT",EDGE,{"derivedFrom":subQ0}),1.0]])]});}
            var Q9;
            {var subQ5=sQuery(id+"F0.wireOp",EDGE,"E23");Q9=makeQuery(id+"F0.imprint","IMPRINT",FACE,{"disambiguationData":[TD([[makeQuery(id+"F0.imprint","IMPRINT",EDGE,{"derivedFrom":subQ5}),-1.0]])]});}
            var Q10;
            {var subQ0=sQuery(id+"F0.wireOp",EDGE,"E36");Q10=makeQuery(id+"F0.imprint","IMPRINT",FACE,{"disambiguationData":[TD([[makeQuery(id+"F0.imprint","IMPRINT",EDGE,{"derivedFrom":subQ0}),-1.0]])]});}
            var Q11;
            {var subQ5=sQuery(id+"F0.wireOp",EDGE,"E19");Q11=makeQuery(id+"F0.imprint","IMPRINT",FACE,{"disambiguationData":[TD([[makeQuery(id+"F0.imprint","IMPRINT",EDGE,{"derivedFrom":subQ5}),-1.0]])]});}
            var Q12;
            {var subQ5=sQuery(id+"F0.wireOp",EDGE,"E20");Q12=makeQuery(id+"F0.imprint","IMPRINT",FACE,{"disambiguationData":[TD([[makeQuery(id+"F0.imprint","IMPRINT",EDGE,{"derivedFrom":subQ5}),1.0]])]});}
            var Q13;
            {var subQ5=sQuery(id+"F0.wireOp",EDGE,"E21");Q13=makeQuery(id+"F0.imprint","IMPRINT",FACE,{"disambiguationData":[TD([[makeQuery(id+"F0.imprint","IMPRINT",EDGE,{"derivedFrom":subQ5}),-1.0]])]});}
            var Q14;
            {var subQ5=sQuery(id+"F0.wireOp",EDGE,"E22");Q14=makeQuery(id+"F0.imprint","IMPRINT",FACE,{"disambiguationData":[TD([[makeQuery(id+"F0.imprint","IMPRINT",EDGE,{"derivedFrom":subQ5}),1.0]])]});}
            var Q15;
            {var subQ0=sQuery(id+"F0.wireOp",EDGE,"E38");Q15=makeQuery(id+"F0.imprint","IMPRINT",FACE,{"disambiguationData":[TD([[makeQuery(id+"F0.imprint","IMPRINT",EDGE,{"derivedFrom":subQ0}),1.0]])]});}
            var Q16;
            {var subQ5=sQuery(id+"F0.wireOp",EDGE,"E35");Q16=makeQuery(id+"F0.imprint","IMPRINT",FACE,{"disambiguationData":[TD([[makeQuery(id+"F0.imprint","IMPRINT",EDGE,{"derivedFrom":subQ5}),1.0]])]});}
            var Q17;
            {var subQ0=sQuery(id+"F0.wireOp",EDGE,"E28");Q17=makeQuery(id+"F0.imprint","IMPRINT",FACE,{"disambiguationData":[TD([[makeQuery(id+"F0.imprint","IMPRINT",EDGE,{"derivedFrom":subQ0}),-1.0]])]});}
            var Q18;
            {var subQ0=sQuery(id+"F0.wireOp",EDGE,"E29");Q18=makeQuery(id+"F0.imprint","IMPRINT",FACE,{"disambiguationData":[TD([[makeQuery(id+"F0.imprint","IMPRINT",EDGE,{"derivedFrom":subQ0}),1.0]])]});}
            var Q19;
            {var subQ5=sQuery(id+"F0.wireOp",EDGE,"E34");Q19=makeQuery(id+"F0.imprint","IMPRINT",FACE,{"disambiguationData":[TD([[makeQuery(id+"F0.imprint","IMPRINT",EDGE,{"derivedFrom":subQ5}),-1.0]])]});}
            var Q20;
            {var subQ0=sQuery(id+"F0.wireOp",EDGE,"E26");Q20=makeQuery(id+"F0.imprint","IMPRINT",FACE,{"disambiguationData":[TD([[makeQuery(id+"F0.imprint","IMPRINT",EDGE,{"derivedFrom":subQ0}),-1.0]])]});}
            var Q21;
            {var subQ5=sQuery(id+"F0.wireOp",EDGE,"E33");Q21=makeQuery(id+"F0.imprint","IMPRINT",FACE,{"disambiguationData":[TD([[makeQuery(id+"F0.imprint","IMPRINT",EDGE,{"derivedFrom":subQ5}),-1.0]])]});}
            var Q22;
            {var subQ0=sQuery(id+"F0.wireOp",EDGE,"E27");Q22=makeQuery(id+"F0.imprint","IMPRINT",FACE,{"disambiguationData":[TD([[makeQuery(id+"F0.imprint","IMPRINT",EDGE,{"derivedFrom":subQ0}),1.0]])]});}
            var Q23;
            {var subQ5=sQuery(id+"F0.wireOp",EDGE,"E32");Q23=makeQuery(id+"F0.imprint","IMPRINT",FACE,{"disambiguationData":[TD([[makeQuery(id+"F0.imprint","IMPRINT",EDGE,{"derivedFrom":subQ5}),1.0]])]});}
            var Q24;
            {var subQ0=sQuery(id+"F0.wireOp",EDGE,"E16.3");var subQ1=sQuery(id+"F0.wireOp",EDGE,"E0");var subQ2=makeQuery(id+"F0.imprint","INTERSECT",VERTEX,{"disambiguationData":[OD(1.0)],"derivedFrom":[subQ1,subQ0]});Q24=makeQuery(id+"F0.imprint","IMPRINT",FACE,{"disambiguationData":[TD([[makeQuery(id+"F0.imprint","IMPRINT",EDGE,{"disambiguationData":[TD([[subQ2,-1.0]])],"derivedFrom":subQ1}),-1.0]])]});}
            var Q25;
            {var subQ0=sQuery(id+"F0.wireOp",EDGE,"E14.4");var subQ1=sQuery(id+"F0.wireOp",EDGE,"E0");var subQ2=makeQuery(id+"F0.imprint","INTERSECT",VERTEX,{"disambiguationData":[OD(0.0)],"derivedFrom":[subQ1,subQ0]});Q25=makeQuery(id+"F0.imprint","IMPRINT",FACE,{"disambiguationData":[TD([[makeQuery(id+"F0.imprint","IMPRINT",EDGE,{"disambiguationData":[TD([[subQ2,-1.0]])],"derivedFrom":subQ1}),-1.0]])]});}
            var Q26;
            {var subQ0=sQuery(id+"F0.wireOp",EDGE,"E16.5");var subQ1=sQuery(id+"F0.wireOp",EDGE,"E0");var subQ2=makeQuery(id+"F0.imprint","INTERSECT",VERTEX,{"disambiguationData":[OD(1.0)],"derivedFrom":[subQ1,subQ0]});Q26=makeQuery(id+"F0.imprint","IMPRINT",FACE,{"disambiguationData":[TD([[makeQuery(id+"F0.imprint","IMPRINT",EDGE,{"disambiguationData":[TD([[subQ2,-1.0]])],"derivedFrom":subQ1}),-1.0]])]});}
            var Q27;
            {var subQ0=sQuery(id+"F0.wireOp",EDGE,"E14.1");var subQ1=sQuery(id+"F0.wireOp",EDGE,"E0");var subQ2=makeQuery(id+"F0.imprint","INTERSECT",VERTEX,{"disambiguationData":[OD(1.0)],"derivedFrom":[subQ1,subQ0]});Q27=makeQuery(id+"F0.imprint","IMPRINT",FACE,{"disambiguationData":[TD([[makeQuery(id+"F0.imprint","IMPRINT",EDGE,{"disambiguationData":[TD([[subQ2,-1.0]])],"derivedFrom":subQ1}),-1.0]])]});}
            var Q28;
            {var subQ0=sQuery(id+"F0.wireOp",EDGE,"E14.0");var subQ1=sQuery(id+"F0.wireOp",EDGE,"E0");var subQ2=makeQuery(id+"F0.imprint","INTERSECT",VERTEX,{"disambiguationData":[OD(0.0)],"derivedFrom":[subQ1,subQ0]});Q28=makeQuery(id+"F0.imprint","IMPRINT",FACE,{"disambiguationData":[TD([[makeQuery(id+"F0.imprint","IMPRINT",EDGE,{"disambiguationData":[TD([[subQ2,-1.0]])],"derivedFrom":subQ1}),-1.0]])]});}
            var Q29;
            {var subQ0=sQuery(id+"F0.wireOp",EDGE,"E16.2");var subQ1=sQuery(id+"F0.wireOp",EDGE,"E0");var subQ2=makeQuery(id+"F0.imprint","INTERSECT",VERTEX,{"disambiguationData":[OD(0.0)],"derivedFrom":[subQ1,subQ0]});Q29=makeQuery(id+"F0.imprint","IMPRINT",FACE,{"disambiguationData":[TD([[makeQuery(id+"F0.imprint","IMPRINT",EDGE,{"disambiguationData":[TD([[subQ2,-1.0]])],"derivedFrom":subQ1}),-1.0]])]});}
            extrude(context, id + "F4", {"entities" : qUnion([Q0, Q1, Q2, Q3, Q4, Q5, Q6, Q7, Q8, Q9, Q10, Q11, Q12, Q13, Q14, Q15, Q16, Q17, Q18, Q19, Q20, Q21, Q22, Q23, Q24, Q25, Q26, Q27, Q28, Q29]), "operationType" : NewBodyOperationType.ADD, "endBound" : BoundingType.SYMMETRIC, "depth" : 0.01 * mm});
        }
    });
